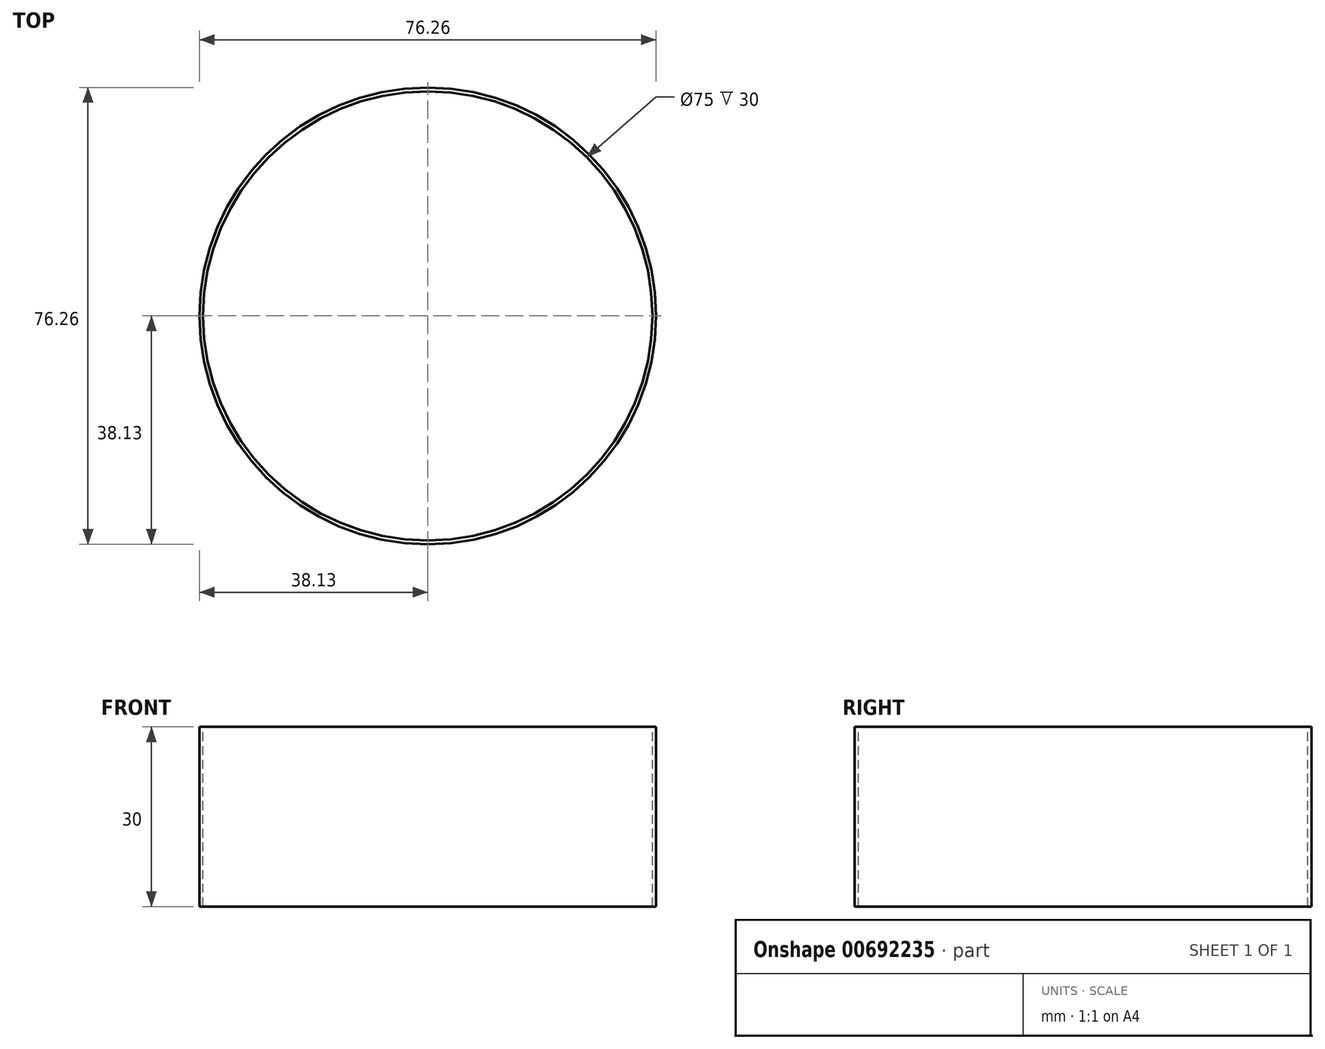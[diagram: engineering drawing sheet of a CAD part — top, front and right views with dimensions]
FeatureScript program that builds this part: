
annotation { "Feature Type Name" : "Feature", "Feature Type Description" : "" }
export const myFeature = defineFeature(function(context is Context, id is Id, definition is map)
    precondition{}
    {
        {
            var Q0;
            Q0=qCreatedBy(makeId("Front.planeOp"),FACE);
            var sketch = newSketch(context, id + "F0", { "sketchPlane" : qUnion([Q0])});
            skLineSegment(sketch, "E0", {"start": v(-38.12, 30) * mm, "end": v(-38.12, 0) * mm});
            skLineSegment(sketch, "E1", {"start": v(-37.5, 0) * mm, "end": v(-37.5, 30) * mm});
            skLineSegment(sketch, "E2", {"start": v(-37.5, 30) * mm, "end": v(-38.12, 30) * mm});
            skLineSegment(sketch, "E3", {"start": v(-37.5, 0) * mm, "end": v(-38.12, 0) * mm});
            skLineSegment(sketch, "E4", {"start": v(0, 0) * mm, "end": v(0, -12.3) * mm});
            skSolve(sketch);
        }
        {
            var Q0;
            Q0 = qSketchRegion(id + "F0", true);
            var Q1;
            Q1=sQuery(id+"F0.wireOp",EDGE,"E4");
            revolve(context, id + "F1", {"surfaceOperationType" : NewSurfaceOperationType.NEW, "entities" : qUnion([Q0]), "axis" : qUnion([Q1]), "revolveType" : RevolveType.FULL});
        }
    });
